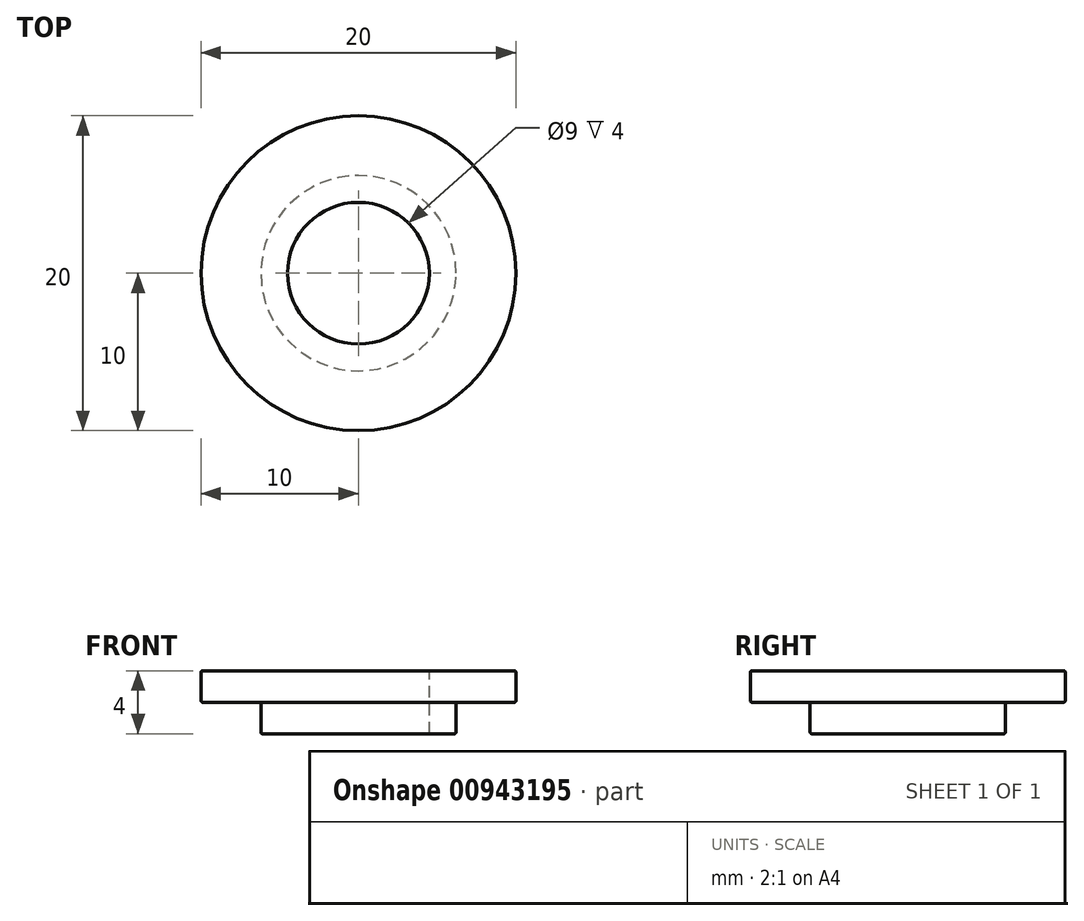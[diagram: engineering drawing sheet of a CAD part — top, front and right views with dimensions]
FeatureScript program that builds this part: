
annotation { "Feature Type Name" : "Feature", "Feature Type Description" : "" }
export const myFeature = defineFeature(function(context is Context, id is Id, definition is map)
    precondition{}
    {
        {
            var Q0;
            Q0=qCreatedBy(makeId("Top.planeOp"),FACE);
            var sketch = newSketch(context, id + "F0", { "sketchPlane" : qUnion([Q0])});
            skCircle(sketch, "E0", {"center": v(0, 0) * mm, "radius": 6.2 * mm});
            skSolve(sketch);
        }
        {
            var Q0;
            Q0=qSketchRegion(id+"F0",true);
            extrude(context, id + "F1", {"entities" : qUnion([Q0]), "depth" : 2 * mm, "offsetDistance" : 25 * mm});
        }
        {
            var Q0;
            Q0=makeQuery(id+"F1.opExtrude","CAP_FACE",FACE,{"disambiguationData":[OSD([sQuery(id+"F0.wireOp",EDGE,"E0")])],"isStart":false});
            var sketch = newSketch(context, id + "F2", { "sketchPlane" : qUnion([Q0])});
            skCircle(sketch, "E1", {"center": v(0, 0) * mm, "radius": 10 * mm});
            skSolve(sketch);
        }
        {
            var Q0;
            Q0=makeQuery(id+"F2.imprint","IMPRINT",FACE,{"disambiguationData":[TD([[makeQuery(id+"F2.imprint","IMPRINT",EDGE,{"derivedFrom":sQuery(id+"F2.wireOp",EDGE,"E1")}),1.0]])]});
            var Q1;
            Q1=makeQuery(id+"F2.imprint","IMPRINT",FACE,{"disambiguationData":[TD([[makeQuery(id+"F2.imprint","IMPRINT",EDGE,{"derivedFrom":makeQuery(id+"F1.opExtrude","CAP_EDGE",EDGE,{"disambiguationData":[OSD([sQuery(id+"F0.wireOp",EDGE,"E0")])],"isStart":false})}),1.0]])]});
            extrude(context, id + "F3", {"entities" : qUnion([Q0, Q1]), "operationType" : NewBodyOperationType.ADD, "depth" : 2 * mm, "offsetDistance" : 25 * mm});
        }
        {
            var Q0;
            Q0=makeQuery(id+"F3.opExtrude","CAP_FACE",FACE,{"disambiguationData":[OSD([sQuery(id+"F2.wireOp",EDGE,"E1")])],"isStart":false});
            var sketch = newSketch(context, id + "F4", { "sketchPlane" : qUnion([Q0])});
            skPoint(sketch, "E2", {"position": v(0, 0) * mm});
            skSolve(sketch);
        }
        {
            var Q0;
            Q0=sQuery(id+"F4.wireOp",VERTEX,"E2");
            var Q1;
            Q1=makeQuery(id+"F1.opExtrude","SWEPT_BODY",BODY,{"disambiguationData":[OSD([sQuery(id+"F0.wireOp",EDGE,"E0")])]});
            hole(context, id + "F5", {"style" : HoleStyle.SIMPLE, "endStyle" : HoleEndStyle.THROUGH, "holeDiameter" : 9 * mm, "majorDiameter" : 8 * mm, "isTappedThrough" : true, "tappedDepth" : 12 * mm, "tapClearance" : 3, "locations" : qUnion([Q0]), "scope" : qUnion([Q1])});
        }
        {
            var Q0;
            Q0=makeQuery(id+"F3.opExtrude","CAP_EDGE",EDGE,{"disambiguationData":[OSD([sQuery(id+"F2.wireOp",EDGE,"E1")])],"isStart":false});
            var Q1;
            Q1=makeQuery(id+"F3.opExtrude","CAP_EDGE",EDGE,{"disambiguationData":[OSD([sQuery(id+"F2.wireOp",EDGE,"E1")])],"isStart":true});
            var Q2;
            Q2=makeQuery(id+"F1.opExtrude","CAP_EDGE",EDGE,{"disambiguationData":[OSD([sQuery(id+"F0.wireOp",EDGE,"E0")])],"isStart":true});
            var Q3;
            Q3=makeQuery(id+"F1.opExtrude","CAP_EDGE",EDGE,{"disambiguationData":[OSD([sQuery(id+"F0.wireOp",EDGE,"E0")])],"isStart":false});
            var Q4;
            Q4=makeQuery(id+"F5.hole-0.boolean.opBoolean","INTERSECT",EDGE,{"derivedFrom":[makeQuery(id+"F1.opExtrude","CAP_FACE",FACE,{"disambiguationData":[OSD([sQuery(id+"F0.wireOp",EDGE,"E0")])],"isStart":true}),makeQuery(id+"F5.hole-0.opRevolve","SWEPT_FACE",FACE,{"disambiguationData":[OSD([sQuery(id+"F5.hole-0.sketch.wireOp",EDGE,"core_line_2")])]})]});
            var Q5;
            Q5=makeQuery(id+"F5.hole-0.boolean.opBoolean","COPY",EDGE,{"derivedFrom":makeQuery(id+"F5.hole-0.opRevolve","SWEPT_EDGE",EDGE,{"disambiguationData":[OSD([sQuery(id+"F5.hole-0.sketch.wireOp",EDGE,"core_line_2"),sQuery(id+"F5.hole-0.sketch.wireOp",EDGE,"core_line_3")])]})});
            fillet(context, id + "F6", {"entities" : qUnion([Q0, Q1, Q2, Q3, Q4, Q5]), "radius" : 0.1 * mm, "tangentPropagation" : true, "allowEdgeOverflow" : false});
        }
    });
